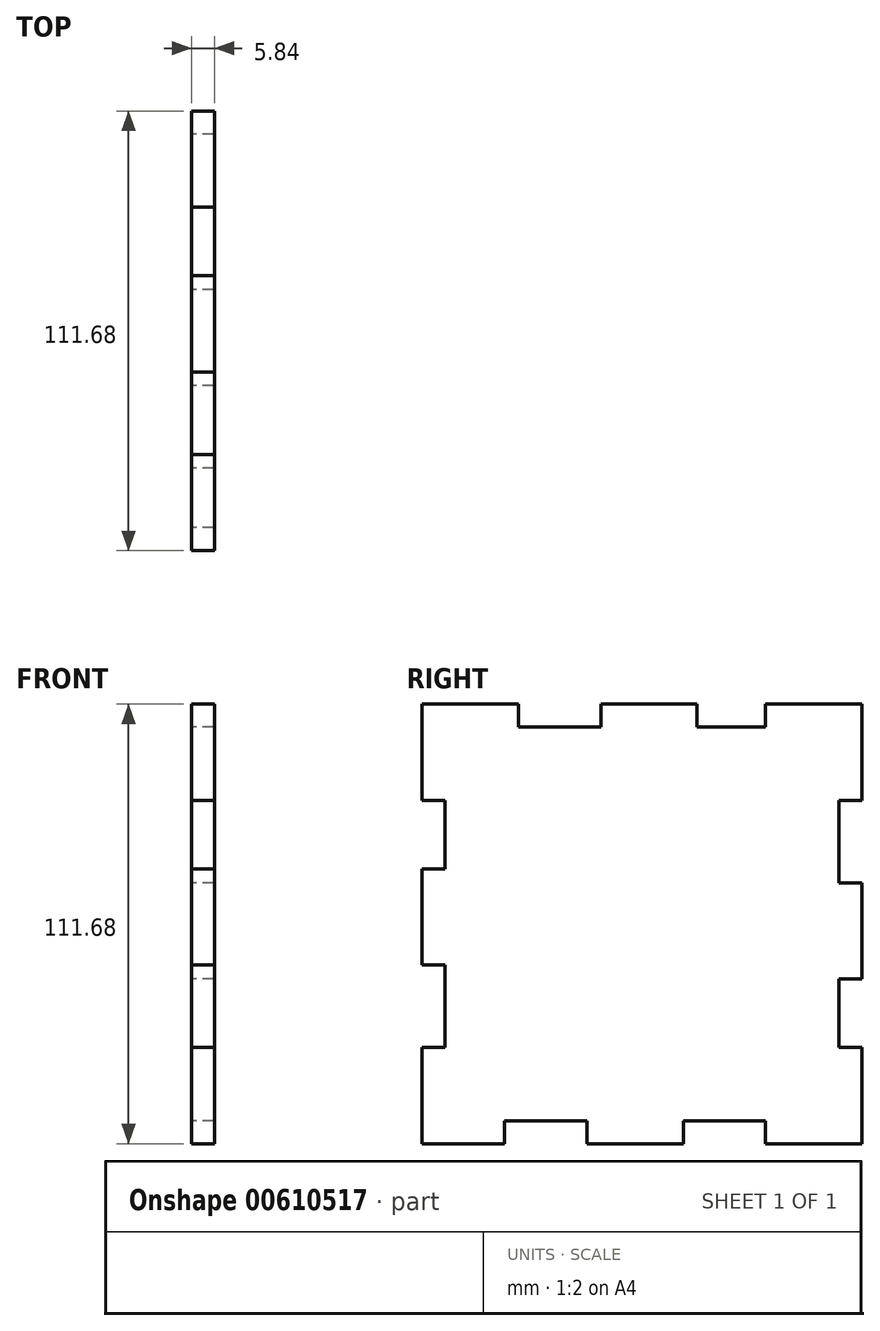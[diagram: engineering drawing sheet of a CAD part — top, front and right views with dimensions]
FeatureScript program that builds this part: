
annotation { "Feature Type Name" : "Feature", "Feature Type Description" : "" }
export const myFeature = defineFeature(function(context is Context, id is Id, definition is map)
    precondition{}
    {
        {
            var Q0;
            Q0=qCreatedBy(makeId("Right.planeOp"),FACE);
            var sketch = newSketch(context, id + "F0", { "sketchPlane" : qUnion([Q0])});
            skLineSegment(sketch, "E0.bottom", {"start": v(50, 50) * mm, "end": v(-50, 50) * mm});
            skLineSegment(sketch, "E0.top", {"start": v(50, -50) * mm, "end": v(-50, -50) * mm});
            skLineSegment(sketch, "E0.left", {"start": v(50, 50) * mm, "end": v(50, -50) * mm});
            skLineSegment(sketch, "E0.right", {"start": v(-50, 50) * mm, "end": v(-50, -50) * mm});
            skPoint(sketch, "E0.middle", {"position": v(0, 0) * mm});
            skLineSegment(sketch, "E1.bottom", {"start": v(-55.84, 55.84) * mm, "end": v(-31.4, 55.84) * mm});
            skLineSegment(sketch, "E1.top", {"start": v(-55.84, -55.84) * mm, "end": v(-34.9, -55.84) * mm});
            skLineSegment(sketch, "E1.left", {"start": v(-55.84, 55.84) * mm, "end": v(-55.84, 31.4) * mm});
            skLineSegment(sketch, "E1.right", {"start": v(55.84, 55.84) * mm, "end": v(55.84, 31.4) * mm});
            skLineSegment(sketch, "E2.bottom", {"start": v(-10.47, 50) * mm, "end": v(13.97, 50) * mm});
            skLineSegment(sketch, "E2.top", {"start": v(-10.47, 55.84) * mm, "end": v(13.97, 55.84) * mm});
            skLineSegment(sketch, "E2.left", {"start": v(-10.47, 50) * mm, "end": v(-10.47, 55.84) * mm});
            skLineSegment(sketch, "E2.right", {"start": v(13.97, 50) * mm, "end": v(13.97, 55.84) * mm});
            skLineSegment(sketch, "E3.right", {"start": v(-31.4, 55.84) * mm, "end": v(-31.4, 50) * mm});
            skLineSegment(sketch, "E4.top", {"start": v(13.97, 50) * mm, "end": v(31.4, 50) * mm});
            skLineSegment(sketch, "E4.left", {"start": v(13.97, 55.84) * mm, "end": v(13.97, 50) * mm});
            skLineSegment(sketch, "E4.right", {"start": v(31.4, 55.84) * mm, "end": v(31.4, 50) * mm});
            skLineSegment(sketch, "E5.bottom", {"start": v(-50, 31.4) * mm, "end": v(-55.84, 31.4) * mm});
            skLineSegment(sketch, "E5.left", {"start": v(-50, 31.4) * mm, "end": v(-50, 13.97) * mm});
            skLineSegment(sketch, "E6.bottom", {"start": v(-55.84, 55.84) * mm, "end": v(-55.84, 55.84) * mm});
            skLineSegment(sketch, "E6.top", {"start": v(-55.84, 31.4) * mm, "end": v(-50, 31.4) * mm});
            skLineSegment(sketch, "E7.bottom", {"start": v(-55.84, -31.4) * mm, "end": v(-50, -31.4) * mm});
            skLineSegment(sketch, "E8.left", {"start": v(-55.84, -55.84) * mm, "end": v(-55.84, -31.4) * mm});
            skLineSegment(sketch, "E9.bottom", {"start": v(-13.97, -55.84) * mm, "end": v(10.47, -55.84) * mm});
            skLineSegment(sketch, "E9.top", {"start": v(-13.97, -50) * mm, "end": v(10.47, -50) * mm});
            skLineSegment(sketch, "E9.left", {"start": v(-13.97, -55.84) * mm, "end": v(-13.97, -50) * mm});
            skLineSegment(sketch, "E9.right", {"start": v(10.47, -55.84) * mm, "end": v(10.47, -50) * mm});
            skLineSegment(sketch, "E10.top", {"start": v(-13.97, -50) * mm, "end": v(-34.9, -50) * mm});
            skLineSegment(sketch, "E10.right", {"start": v(-34.9, -55.84) * mm, "end": v(-34.9, -50) * mm});
            skLineSegment(sketch, "E11.top", {"start": v(10.47, -50) * mm, "end": v(31.4, -50) * mm});
            skLineSegment(sketch, "E11.right", {"start": v(31.4, -55.84) * mm, "end": v(31.4, -50) * mm});
            skLineSegment(sketch, "E12.bottom", {"start": v(31.4, -55.84) * mm, "end": v(55.84, -55.84) * mm});
            skLineSegment(sketch, "E12.right", {"start": v(55.84, -55.84) * mm, "end": v(55.84, -50) * mm});
            skLineSegment(sketch, "E13.bottom", {"start": v(56.02, -55.84) * mm, "end": v(55.84, -55.84) * mm});
            skLineSegment(sketch, "E13.top", {"start": v(55.84, -31.4) * mm, "end": v(50, -31.4) * mm});
            skLineSegment(sketch, "E13.left", {"start": v(55.84, -55.84) * mm, "end": v(55.84, -31.4) * mm});
            skLineSegment(sketch, "E14.top", {"start": v(55.84, -13.97) * mm, "end": v(50, -13.97) * mm});
            skLineSegment(sketch, "E14.right", {"start": v(50, -31.4) * mm, "end": v(50, -13.97) * mm});
            skLineSegment(sketch, "E15.bottom", {"start": v(50, -13.97) * mm, "end": v(55.84, -13.97) * mm});
            skLineSegment(sketch, "E15.top", {"start": v(50, 10.47) * mm, "end": v(55.84, 10.47) * mm});
            skLineSegment(sketch, "E15.right", {"start": v(55.84, -13.97) * mm, "end": v(55.84, 10.47) * mm});
            skLineSegment(sketch, "E16.top", {"start": v(50, 31.4) * mm, "end": v(55.84, 31.4) * mm});
            skLineSegment(sketch, "E16.left", {"start": v(50, 10.47) * mm, "end": v(50, 31.4) * mm});
            skLineSegment(sketch, "E17.trimOffspring", {"start": v(31.4, 55.84) * mm, "end": v(55.84, 55.84) * mm});
            skLineSegment(sketch, "E18.trimOffspring", {"start": v(55.84, 10.47) * mm, "end": v(55.84, -13.97) * mm});
            skLineSegment(sketch, "E19.trimOffspring", {"start": v(55.84, -31.4) * mm, "end": v(55.84, -55.84) * mm});
            skLineSegment(sketch, "E20.trimOffspring", {"start": v(-55.84, -31.4) * mm, "end": v(-55.84, -55.84) * mm});
            skLineSegment(sketch, "E21.bottom", {"start": v(-55.84, 13.97) * mm, "end": v(-50, 13.97) * mm});
            skLineSegment(sketch, "E21.top", {"start": v(-55.84, -10.47) * mm, "end": v(-50, -10.47) * mm});
            skLineSegment(sketch, "E21.left", {"start": v(-55.84, 13.97) * mm, "end": v(-55.84, -10.47) * mm});
            skLineSegment(sketch, "E21.right", {"start": v(-50, 13.97) * mm, "end": v(-50, -10.47) * mm});
            skSolve(sketch);
        }
        {
            var Q0;
            Q0=qSketchRegion(id+"F0",true);
            extrude(context, id + "F1", {"entities" : qUnion([Q0]), "depth" : 5.84 * mm, "offsetDistance" : 25 * mm});
        }
    });
